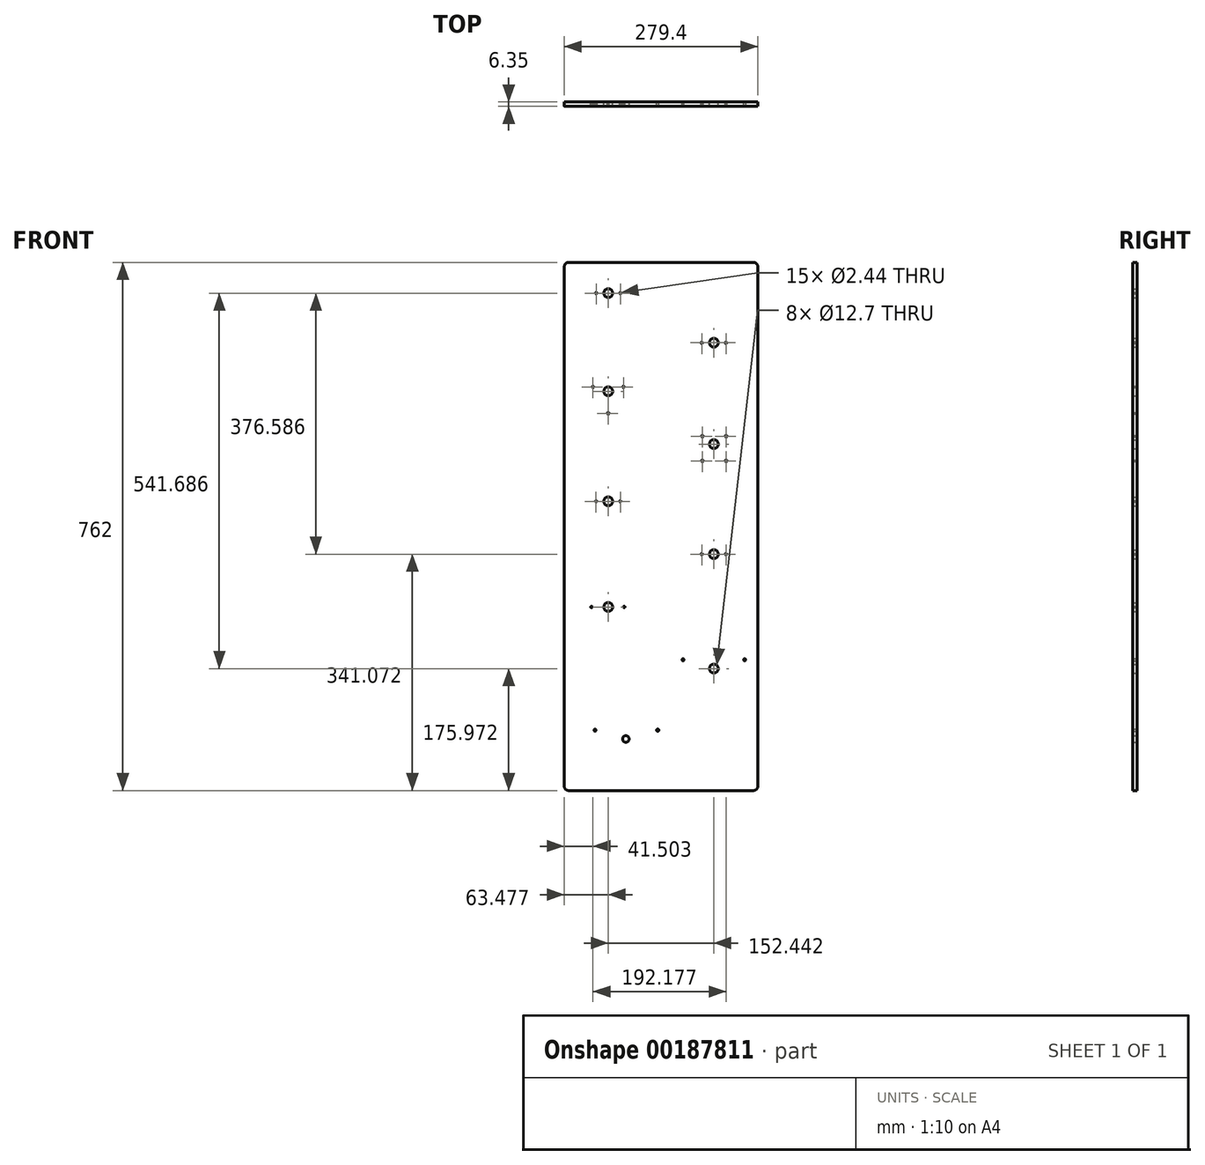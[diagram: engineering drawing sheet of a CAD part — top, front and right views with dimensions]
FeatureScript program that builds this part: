
annotation { "Feature Type Name" : "Feature", "Feature Type Description" : "" }
export const myFeature = defineFeature(function(context is Context, id is Id, definition is map)
    precondition{}
    {
        {
            var Q0;
            Q0=qCreatedBy(makeId("Front.planeOp"),FACE);
            var sketch = newSketch(context, id + "F0", { "sketchPlane" : qUnion([Q0])});
            skLineSegment(sketch, "E0.bottom", {"start": v(133.35, -381) * mm, "end": v(-133.35, -381) * mm});
            skLineSegment(sketch, "E0.top", {"start": v(133.35, 381) * mm, "end": v(-133.35, 381) * mm});
            skLineSegment(sketch, "E0.left", {"start": v(139.7, -374.65) * mm, "end": v(139.7, 374.65) * mm});
            skLineSegment(sketch, "E0.right", {"start": v(-139.7, -374.65) * mm, "end": v(-139.7, 374.65) * mm});
            skPoint(sketch, "E0.middle", {"position": v(0, 0) * mm});
            skLineSegment(sketch, "E1", {"start": v(-123.46, -293.93) * mm, "end": v(223.85, -293.93) * mm, "construction": true});
            skLineSegment(sketch, "E2", {"start": v(-160.35, -192.33) * mm, "end": v(223.85, -192.33) * mm, "construction": true});
            skLineSegment(sketch, "E3", {"start": v(-128.6, -116.13) * mm, "end": v(223.85, -116.13) * mm, "construction": true});
            skLineSegment(sketch, "E4", {"start": v(-145.33, -39.93) * mm, "end": v(223.85, -39.93) * mm, "construction": true});
            skLineSegment(sketch, "E5", {"start": v(-128.04, 36.27) * mm, "end": v(196.11, 36.27) * mm, "construction": true});
            skLineSegment(sketch, "E6", {"start": v(-133.75, 112.47) * mm, "end": v(194.26, 112.47) * mm, "construction": true});
            skLineSegment(sketch, "E7", {"start": v(-140.9, 188.67) * mm, "end": v(206.4, 188.67) * mm, "construction": true});
            skLineSegment(sketch, "E8", {"start": v(-145.33, 264.87) * mm, "end": v(223.85, 264.87) * mm, "construction": true});
            skLineSegment(sketch, "E9", {"start": v(-151.76, 341.07) * mm, "end": v(223.85, 341.07) * mm, "construction": true});
            skLineSegment(sketch, "E10", {"start": v(-50.8, 400.05) * mm, "end": v(-50.8, -398.76) * mm, "construction": true});
            skLineSegment(sketch, "E11", {"start": v(76.2, 397.48) * mm, "end": v(76.2, -396.2) * mm, "construction": true});
            skLineSegment(sketch, "E12", {"start": v(0, 423.93) * mm, "end": v(0, -430.77) * mm, "construction": true});
            skPoint(sketch, "E12.startSnap0", {"position": v(0, 381) * mm});
            skCircle(sketch, "E13", {"center": v(-50.8, -293.93) * mm, "radius": 79.38 * mm, "construction": true});
            skCircle(sketch, "E14", {"center": v(76.2, -192.33) * mm, "radius": 53.98 * mm, "construction": true});
            skLineSegment(sketch, "E15", {"start": v(-76.2, 412.75) * mm, "end": v(-76.2, -262.46) * mm, "construction": true});
            skCircle(sketch, "E16", {"center": v(-76.2, 341.07) * mm, "radius": 22.86 * mm, "construction": true});
            skCircle(sketch, "E17", {"center": v(76.2, 264.87) * mm, "radius": 22.86 * mm, "construction": true});
            skCircle(sketch, "E18", {"center": v(-76.2, 188.67) * mm, "radius": 33.02 * mm, "construction": true});
            skCircle(sketch, "E19", {"center": v(-76.2, 36.27) * mm, "radius": 22.86 * mm, "construction": true});
            skCircle(sketch, "E20", {"center": v(76.2, -39.93) * mm, "radius": 22.86 * mm, "construction": true});
            skCircle(sketch, "E21", {"center": v(-76.2, -116.13) * mm, "radius": 33.02 * mm, "construction": true});
            skLineSegment(sketch, "E22.bottom", {"start": v(111.13, 77.55) * mm, "end": v(41.28, 77.55) * mm, "construction": true});
            skLineSegment(sketch, "E22.top", {"start": v(111.13, 147.4) * mm, "end": v(41.28, 147.4) * mm, "construction": true});
            skLineSegment(sketch, "E22.left", {"start": v(111.13, 77.55) * mm, "end": v(111.13, 147.4) * mm, "construction": true});
            skLineSegment(sketch, "E22.right", {"start": v(41.28, 77.55) * mm, "end": v(41.28, 147.4) * mm, "construction": true});
            skPoint(sketch, "E22.middle", {"position": v(76.2, 112.47) * mm});
            skCircle(sketch, "E23", {"center": v(-95.25, -293.93) * mm, "radius": 1.56 * mm});
            skCircle(sketch, "E24", {"center": v(-4.79, -293.93) * mm, "radius": 1.56 * mm});
            skCircle(sketch, "E25", {"center": v(-50.8, -306.63) * mm, "radius": 4.76 * mm});
            skCircle(sketch, "E26", {"center": v(31.75, -192.33) * mm, "radius": 1.56 * mm});
            skCircle(sketch, "E27", {"center": v(120.65, -192.33) * mm, "radius": 1.56 * mm});
            skCircle(sketch, "E28", {"center": v(76.2, -205.03) * mm, "radius": 6.35 * mm});
            skCircle(sketch, "E29", {"center": v(-76.2, -116.13) * mm, "radius": 6.35 * mm});
            skCircle(sketch, "E30", {"center": v(-100.33, -116.13) * mm, "radius": 1.14 * mm});
            skCircle(sketch, "E31", {"center": v(-53.21, -116.13) * mm, "radius": 1.14 * mm});
            skCircle(sketch, "E32", {"center": v(76.2, -39.93) * mm, "radius": 6.35 * mm});
            skCircle(sketch, "E33", {"center": v(58.74, -39.93) * mm, "radius": 1.22 * mm});
            skCircle(sketch, "E34", {"center": v(93.66, -39.93) * mm, "radius": 1.22 * mm});
            skCircle(sketch, "E35", {"center": v(-76.22, 36.3) * mm, "radius": 6.35 * mm});
            skCircle(sketch, "E36", {"center": v(-93.69, 36.3) * mm, "radius": 1.22 * mm});
            skCircle(sketch, "E37", {"center": v(-58.76, 36.3) * mm, "radius": 1.22 * mm});
            skCircle(sketch, "E38", {"center": v(76.22, 265.02) * mm, "radius": 6.35 * mm});
            skCircle(sketch, "E39", {"center": v(58.76, 265.02) * mm, "radius": 1.22 * mm});
            skCircle(sketch, "E40", {"center": v(93.68, 265.02) * mm, "radius": 1.22 * mm});
            skCircle(sketch, "E41", {"center": v(-76.15, 336.66) * mm, "radius": 6.35 * mm});
            skCircle(sketch, "E42", {"center": v(-93.61, 336.66) * mm, "radius": 1.22 * mm});
            skCircle(sketch, "E43", {"center": v(-58.69, 336.66) * mm, "radius": 1.22 * mm});
            skCircle(sketch, "E44", {"center": v(-76.2, 188.67) * mm, "radius": 25.4 * mm, "construction": true});
            skCircle(sketch, "E45", {"center": v(-76.2, 163.27) * mm, "radius": 1.22 * mm});
            skLineSegment(sketch, "E46", {"start": v(-76.2, 188.67) * mm, "end": v(-116.38, 211.87) * mm, "construction": true});
            skLineSegment(sketch, "E47", {"start": v(-76.2, 188.67) * mm, "end": v(-33.94, 213.07) * mm, "construction": true});
            skCircle(sketch, "E48", {"center": v(-98.2, 201.37) * mm, "radius": 1.22 * mm});
            skCircle(sketch, "E49", {"center": v(-54.2, 201.37) * mm, "radius": 1.22 * mm});
            skCircle(sketch, "E50", {"center": v(-76.2, 195.02) * mm, "radius": 6.35 * mm});
            skCircle(sketch, "E51", {"center": v(59.64, 130.25) * mm, "radius": 1.22 * mm});
            skCircle(sketch, "E52", {"center": v(93.98, 130.25) * mm, "radius": 1.22 * mm});
            skPoint(sketch, "E53.visualSharp", {"position": v(-139.7, 381) * mm});
            skArc(sketch, "E53.filletArc", {"start": v(-133.35, 381) * mm, "mid": v(-137.84, 379.14) * mm, "end": v(-139.7, 374.65) * mm});
            skPoint(sketch, "E54.visualSharp", {"position": v(139.7, 381) * mm});
            skArc(sketch, "E54.filletArc", {"start": v(139.7, 374.65) * mm, "mid": v(137.84, 379.14) * mm, "end": v(133.35, 381) * mm});
            skPoint(sketch, "E55.visualSharp", {"position": v(139.7, -381) * mm});
            skArc(sketch, "E55.filletArc", {"start": v(133.35, -381) * mm, "mid": v(137.84, -379.14) * mm, "end": v(139.7, -374.65) * mm});
            skPoint(sketch, "E56.visualSharp", {"position": v(-139.7, -381) * mm});
            skArc(sketch, "E56.filletArc", {"start": v(-139.7, -374.65) * mm, "mid": v(-137.84, -379.14) * mm, "end": v(-133.35, -381) * mm});
            skCircle(sketch, "E57.MirrorC", {"center": v(93.98, 94.7) * mm, "radius": 1.22 * mm});
            skCircle(sketch, "E58.MirrorC", {"center": v(59.64, 94.7) * mm, "radius": 1.22 * mm});
            skCircle(sketch, "E59", {"center": v(76.2, 118.82) * mm, "radius": 6.35 * mm});
            skSolve(sketch);
        }
        {
            var Q0;
            Q0=qSketchRegion(id+"F0",true);
            extrude(context, id + "F1", {"entities" : qUnion([Q0]), "depth" : 6.35 * mm});
        }
    });
